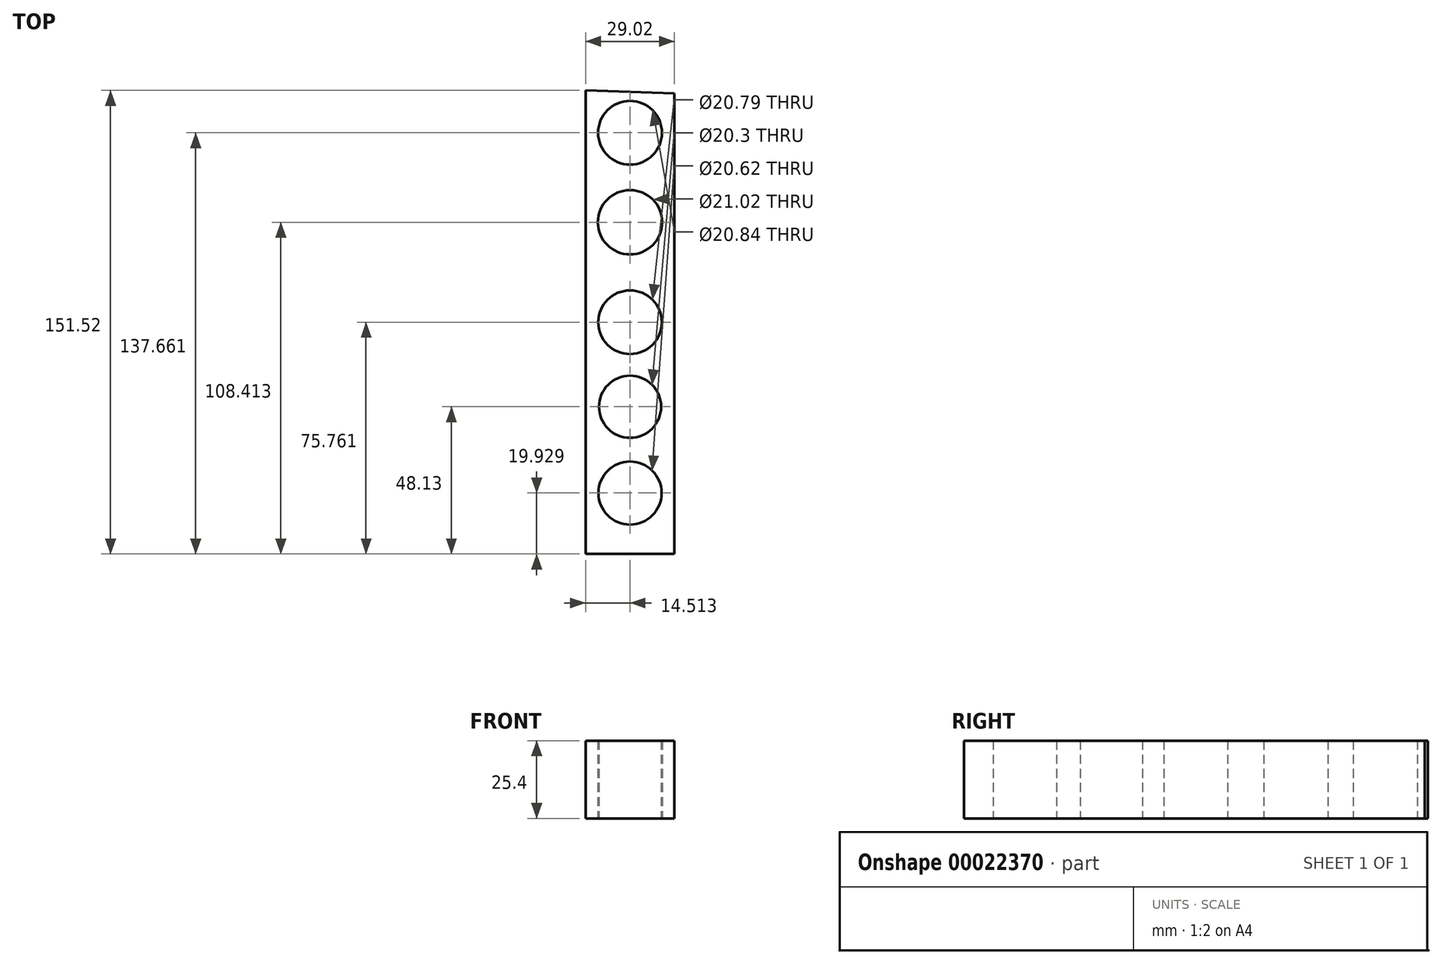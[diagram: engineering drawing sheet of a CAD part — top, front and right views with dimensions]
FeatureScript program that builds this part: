
annotation { "Feature Type Name" : "Feature", "Feature Type Description" : "" }
export const myFeature = defineFeature(function(context is Context, id is Id, definition is map)
    precondition{}
    {
        {
            var Q0;
            Q0=qCreatedBy(makeId("Top.planeOp"),FACE);
            var sketch = newSketch(context, id + "F0", { "sketchPlane" : qUnion([Q0])});
            skLineSegment(sketch, "E0", {"start": v(-76.23, -77.14) * mm, "end": v(-47.1, -77.14) * mm});
            skLineSegment(sketch, "E1", {"start": v(-76.23, -77.14) * mm, "end": v(-76.23, 74.38) * mm});
            skLineSegment(sketch, "E2", {"start": v(-47.2, -77.14) * mm, "end": v(-47.2, 73.4) * mm});
            skLineSegment(sketch, "E3", {"start": v(-76.23, 74.38) * mm, "end": v(-47.2, 73.4) * mm});
            skCircle(sketch, "E4", {"center": v(-61.72, -7.35) * mm, "radius": 1.04 * mm});
            skCircle(sketch, "E5", {"center": v(-61.72, -1.38) * mm, "radius": 10.4 * mm});
            skCircle(sketch, "E6", {"center": v(-61.72, -29.01) * mm, "radius": 10.15 * mm});
            skCircle(sketch, "E7", {"center": v(-61.72, -57.21) * mm, "radius": 10.31 * mm});
            skCircle(sketch, "E8", {"center": v(-61.72, 31.27) * mm, "radius": 10.51 * mm});
            skCircle(sketch, "E9", {"center": v(-61.72, 60.52) * mm, "radius": 10.42 * mm});
            skSolve(sketch);
        }
        {
            var Q0;
            {var subQ1=sQuery(id+"F0.wireOp",EDGE,"E1");Q0=makeQuery(id+"F0.imprint","IMPRINT",FACE,{"disambiguationData":[TD([[makeQuery(id+"F0.imprint","IMPRINT",EDGE,{"derivedFrom":subQ1}),-1.0]])]});}
            extrude(context, id + "F1", {"entities" : qUnion([Q0]), "depth" : 25.4 * mm});
        }
        {
            var Q0;
            {var subQ1=sQuery(id+"F0.wireOp",EDGE,"E1");Q0=makeQuery(id+"F0.imprint","IMPRINT",FACE,{"disambiguationData":[TD([[makeQuery(id+"F0.imprint","IMPRINT",EDGE,{"derivedFrom":subQ1}),-1.0]])]});}
            extrude(context, id + "F2", {"entities" : qUnion([Q0]), "operationType" : NewBodyOperationType.ADD, "depth" : 25.4 * mm});
        }
    });
